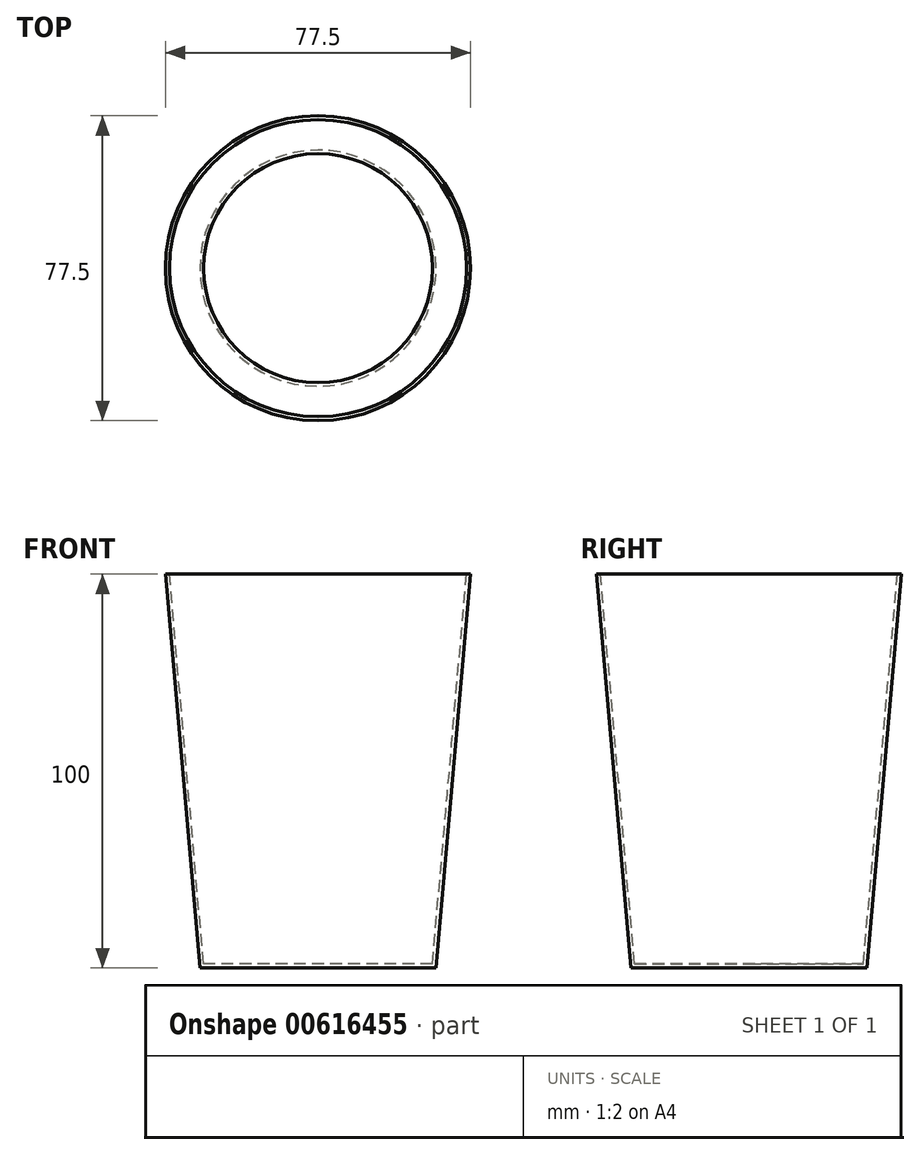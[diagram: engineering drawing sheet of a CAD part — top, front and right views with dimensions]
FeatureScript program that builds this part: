
annotation { "Feature Type Name" : "Feature", "Feature Type Description" : "" }
export const myFeature = defineFeature(function(context is Context, id is Id, definition is map)
    precondition{}
    {
        {
            var Q0;
            Q0=qCreatedBy(makeId("Top.planeOp"),FACE);
            var sketch = newSketch(context, id + "F0", { "sketchPlane" : qUnion([Q0])});
            skCircle(sketch, "E0", {"center": v(0, 0) * mm, "radius": 30 * mm});
            skLineSegment(sketch, "E1", {"start": v(-30, 0) * mm, "end": v(30, 0) * mm, "construction": true});
            skSolve(sketch);
        }
        {
            var Q0;
            Q0=makeQuery(id+"F0.imprint","IMPRINT",FACE,{"disambiguationData":[TD([[makeQuery(id+"F0.imprint","IMPRINT",EDGE,{"derivedFrom":sQuery(id+"F0.wireOp",EDGE,"E0")}),1.0]])]});
            extrude(context, id + "F1", {"entities" : qUnion([Q0]), "depth" : 100 * mm, "offsetDistance" : 25 * mm, "hasDraft" : true, "draftAngle" : 5 * degree});
        }
        {
            var Q0;
            Q0=makeQuery(id+"F1.opExtrude","CAP_FACE",FACE,{"disambiguationData":[OSD([sQuery(id+"F0.wireOp",EDGE,"E0")])],"isStart":false});
            shell(context, id + "F2", {"entities" : qUnion([Q0]), "thickness" : 1 * mm});
        }
    });
